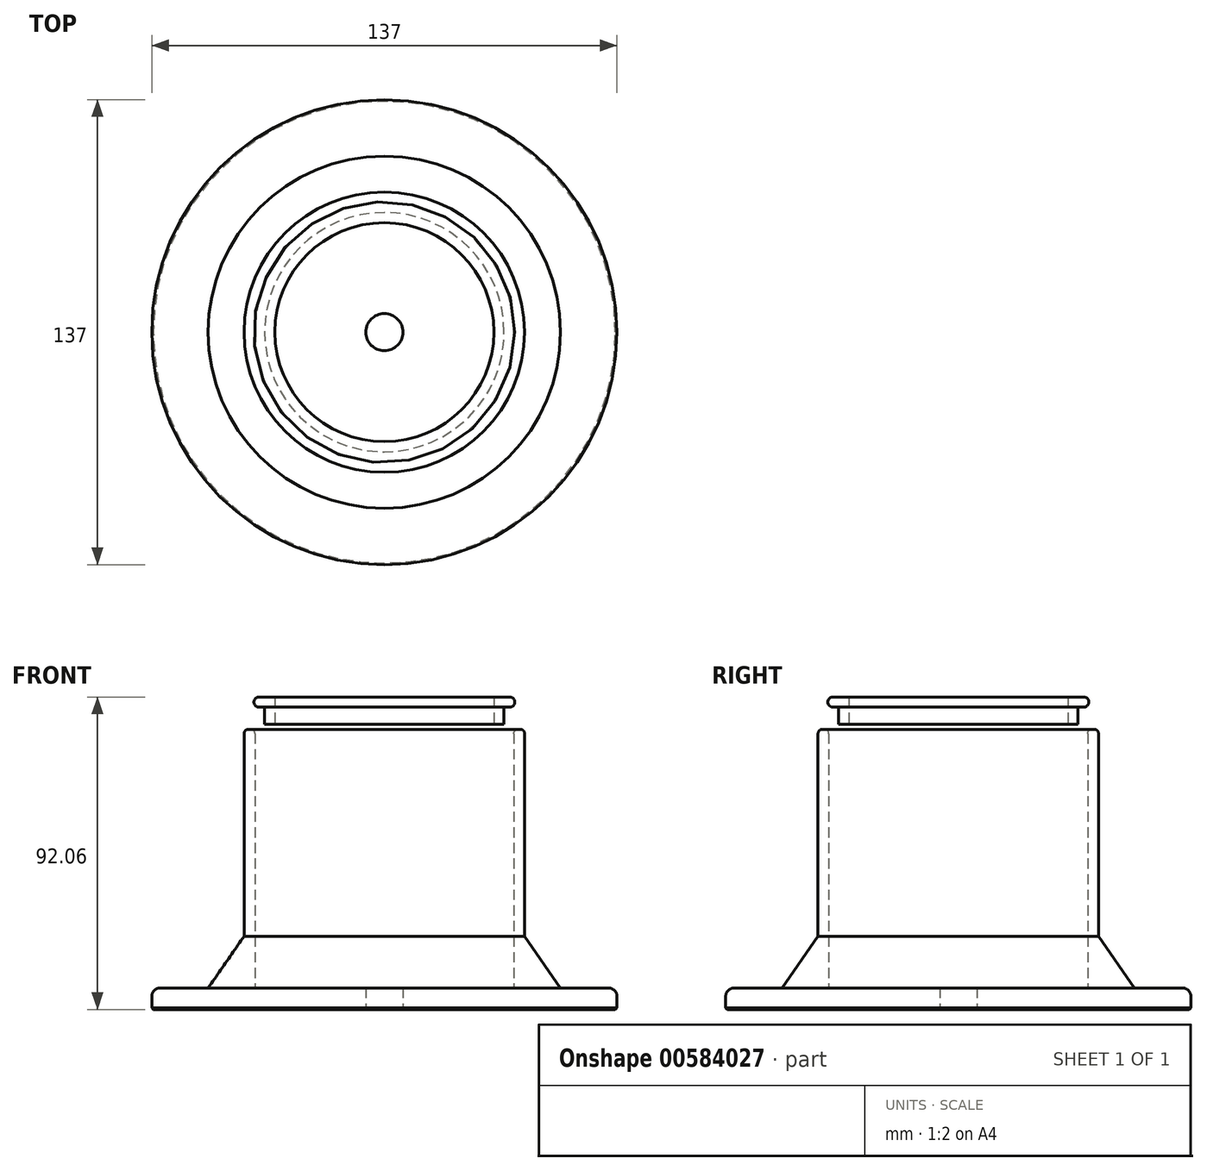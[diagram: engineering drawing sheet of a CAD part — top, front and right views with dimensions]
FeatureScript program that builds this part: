
annotation { "Feature Type Name" : "Feature", "Feature Type Description" : "" }
export const myFeature = defineFeature(function(context is Context, id is Id, definition is map)
    precondition{}
    {
        {
            assignVariable(context, id + "F0", {"name" : "baseheight", "anyValue" : 6.35 * mm});
        }
        {
            assignVariable(context, id + "F1", {"name" : "wallthick", "anyValue" : 3.17 * mm});
        }
        {
            var Q0;
            Q0=qCreatedBy(makeId("Front.planeOp"),FACE);
            var sketch = newSketch(context, id + "F2", { "sketchPlane" : qUnion([Q0])});
            skLineSegment(sketch, "E0", {"start": v(-68.5, 6.35) * mm, "end": v(-68.5, 0) * mm});
            skLineSegment(sketch, "E1", {"start": v(-68.5, 0) * mm, "end": v(0, 0) * mm});
            skLineSegment(sketch, "E2", {"start": v(0, 0) * mm, "end": v(0, 6.35) * mm});
            skLineSegment(sketch, "E3", {"start": v(0, 6.35) * mm, "end": v(-38.12, 6.35) * mm});
            skLineSegment(sketch, "E4", {"start": v(-38.12, 6.35) * mm, "end": v(-38.12, 82.55) * mm});
            skLineSegment(sketch, "E5", {"start": v(-38.12, 82.55) * mm, "end": v(-41.3, 82.55) * mm});
            skLineSegment(sketch, "E6", {"start": v(-41.3, 82.55) * mm, "end": v(-41.3, 21.59) * mm});
            skLineSegment(sketch, "E7", {"start": v(-41.3, 21.59) * mm, "end": v(-51.88, 6.35) * mm});
            skLineSegment(sketch, "E8", {"start": v(-51.88, 6.35) * mm, "end": v(-68.5, 6.35) * mm});
            skSolve(sketch);
        }
        {
            var Q0;
            Q0=qCreatedBy(makeId("Front.planeOp"),FACE);
            var sketch = newSketch(context, id + "F3", { "sketchPlane" : qUnion([Q0])});
            skLineSegment(sketch, "E9", {"start": v(0, 0) * mm, "end": v(0, 82.2) * mm, "construction": true});
            skSolve(sketch);
        }
        {
            var Q0;
            Q0=qCreatedBy(makeId("Front.planeOp"),FACE);
            var sketch = newSketch(context, id + "F4", { "sketchPlane" : qUnion([Q0])});
            skLineSegment(sketch, "E10", {"start": v(-35.25, 84.06) * mm, "end": v(-35.25, 89.06) * mm});
            skLineSegment(sketch, "E11", {"start": v(-35.25, 89.06) * mm, "end": v(-38.43, 89.06) * mm});
            skLineSegment(sketch, "E12", {"start": v(-38.43, 89.06) * mm, "end": v(-38.43, 92.06) * mm});
            skLineSegment(sketch, "E13", {"start": v(-38.43, 92.06) * mm, "end": v(-32.25, 92.06) * mm});
            skLineSegment(sketch, "E14", {"start": v(-32.25, 92.06) * mm, "end": v(-32.25, 84.06) * mm});
            skLineSegment(sketch, "E15", {"start": v(-32.25, 84.06) * mm, "end": v(-35.25, 84.06) * mm});
            skLineSegment(sketch, "E16", {"start": v(0, 68.8) * mm, "end": v(0, 95.4) * mm, "construction": true});
            skLineSegment(sketch, "E17", {"start": v(0, 85.18) * mm, "end": v(-32.25, 85.18) * mm, "construction": true});
            skSolve(sketch);
        }
        {
            var Q0;
            Q0=makeQuery(id+"F2.imprint","IMPRINT",FACE,{"disambiguationData":[TD([[makeQuery(id+"F2.imprint","IMPRINT",EDGE,{"derivedFrom":sQuery(id+"F2.wireOp",EDGE,"E0")}),1.0]])]});
            var Q1;
            Q1=sQuery(id+"F2.wireOp",EDGE,"E2");
            revolve(context, id + "F5", {"entities" : qUnion([Q0]), "axis" : qUnion([Q1]), "revolveType" : RevolveType.FULL});
        }
        {
            var Q0;
            Q0=makeQuery(id+"F5.opRevolve","SWEPT_EDGE",EDGE,{"disambiguationData":[OSD([sQuery(id+"F2.wireOp",EDGE,"E0"),sQuery(id+"F2.wireOp",EDGE,"E8")])]});
            fillet(context, id + "F6", {"entities" : qUnion([Q0]), "radius" : getVariable(context, 'baseheight') * 0.4, "tangentPropagation" : true, "allowEdgeOverflow" : false});
        }
        {
            var Q0;
            Q0=qCreatedBy(makeId("Top.planeOp"),FACE);
            var sketch = newSketch(context, id + "F7", { "sketchPlane" : qUnion([Q0])});
            skCircle(sketch, "E18", {"center": v(0, 0) * mm, "radius": 5.46 * mm});
            skSolve(sketch);
        }
        {
            var Q0;
            Q0 = qSketchRegion(id + "F7", true);
            extrude(context, id + "F8", {"entities" : qUnion([Q0]), "operationType" : NewBodyOperationType.REMOVE, "endBound" : BoundingType.THROUGH_ALL, "depth" : getVariable(context, 'baseheight'), "offsetDistance" : 25 * mm});
        }
        {
            var Q0;
            Q0=makeQuery(id+"F5.opRevolve","SWEPT_EDGE",EDGE,{"disambiguationData":[OSD([sQuery(id+"F2.wireOp",EDGE,"E0"),sQuery(id+"F2.wireOp",EDGE,"E1")])]});
            chamfer(context, id + "F9", {"entities" : qUnion([Q0]), "width" : 0.5 * mm, "tangentPropagation" : true});
        }
        {
            var Q0;
            Q0=makeQuery(id+"F5.opRevolve","SWEPT_EDGE",EDGE,{"disambiguationData":[OSD([sQuery(id+"F2.wireOp",EDGE,"E4"),sQuery(id+"F2.wireOp",EDGE,"E5")])]});
            fillet(context, id + "F10", {"entities" : qUnion([Q0]), "radius" : getVariable(context, 'wallthick') * 0.4, "tangentPropagation" : true, "allowEdgeOverflow" : false});
        }
        {
            var Q0;
            Q0=makeQuery(id+"F5.opRevolve","SWEPT_EDGE",EDGE,{"disambiguationData":[OSD([sQuery(id+"F2.wireOp",EDGE,"E5"),sQuery(id+"F2.wireOp",EDGE,"E6")])]});
            fillet(context, id + "F11", {"entities" : qUnion([Q0]), "radius" : getVariable(context, 'wallthick') * 0.4, "tangentPropagation" : true, "allowEdgeOverflow" : false});
        }
        {
            var Q0;
            Q0 = qSketchRegion(id + "F4", true);
            var Q1;
            Q1=sQuery(id+"F3.wireOp",EDGE,"E9");
            revolve(context, id + "F12", {"entities" : qUnion([Q0]), "axis" : qUnion([Q1]), "revolveType" : RevolveType.FULL});
        }
        {
            var Q0;
            Q0=makeQuery(id+"F12.opRevolve","SWEPT_EDGE",EDGE,{"disambiguationData":[OSD([sQuery(id+"F4.wireOp",EDGE,"E12"),sQuery(id+"F4.wireOp",EDGE,"E13")])]});
            fillet(context, id + "F13", {"entities" : qUnion([Q0]), "radius" : 1.5 * mm, "tangentPropagation" : true, "allowEdgeOverflow" : false});
        }
        {
            var Q0;
            Q0=makeQuery(id+"F12.opRevolve","SWEPT_EDGE",EDGE,{"disambiguationData":[OSD([sQuery(id+"F4.wireOp",EDGE,"E11"),sQuery(id+"F4.wireOp",EDGE,"E12")])]});
            var Q1;
            Q1=makeQuery(id+"F12.opRevolve","SWEPT_FACE",FACE,{"disambiguationData":[OSD([sQuery(id+"F4.wireOp",EDGE,"E12")])]});
            fillet(context, id + "F14", {"entities" : qUnion([Q0, Q1]), "radius" : 1.5 * mm, "tangentPropagation" : true, "allowEdgeOverflow" : false});
        }
    });
